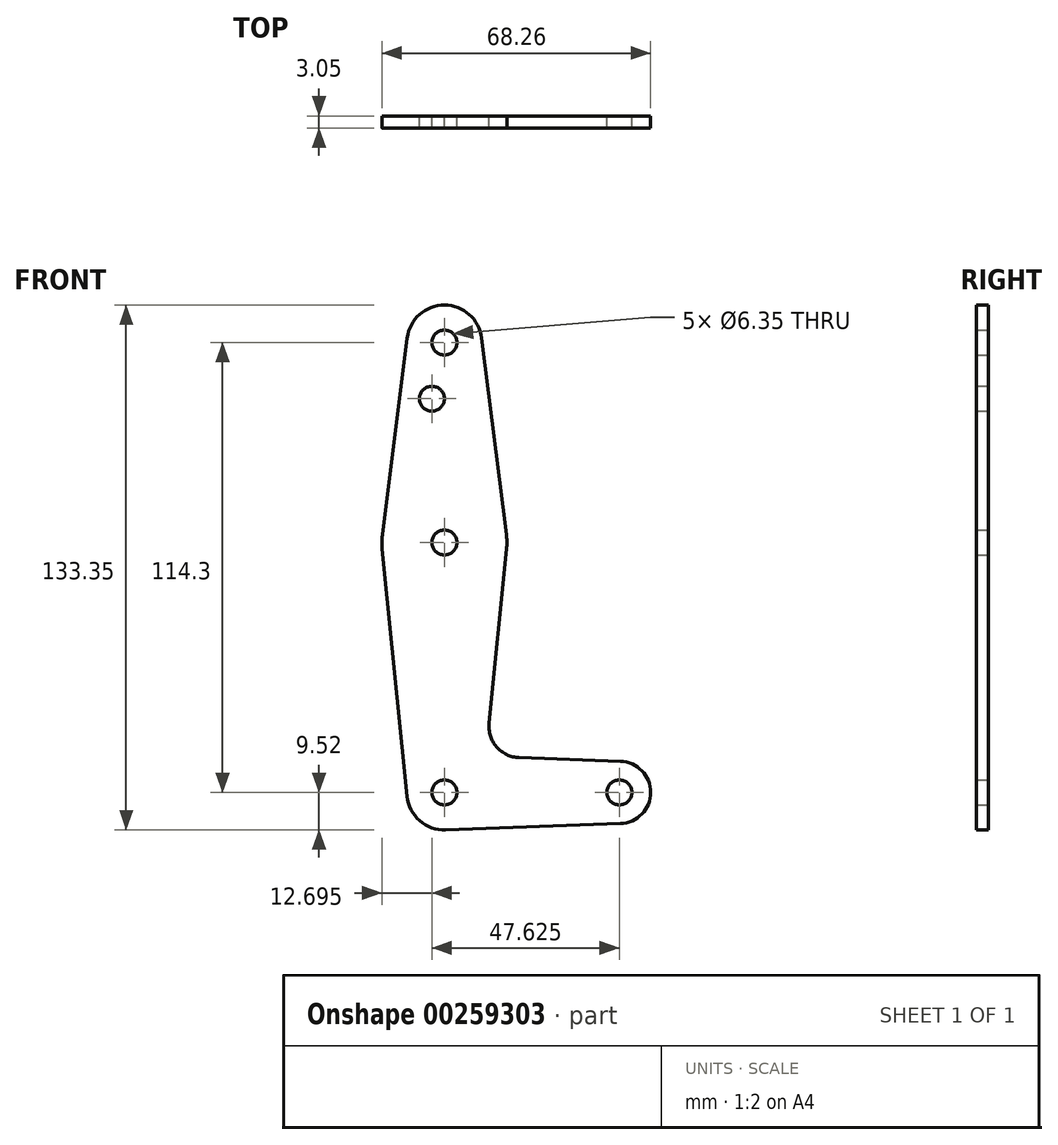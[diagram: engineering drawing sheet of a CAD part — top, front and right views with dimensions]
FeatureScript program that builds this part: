
annotation { "Feature Type Name" : "Feature", "Feature Type Description" : "" }
export const myFeature = defineFeature(function(context is Context, id is Id, definition is map)
    precondition{}
    {
        {
            var Q0;
            Q0=qCreatedBy(makeId("Front.planeOp"),FACE);
            var sketch = newSketch(context, id + "F0", { "sketchPlane" : qUnion([Q0])});
            skLineSegment(sketch, "E0", {"start": v(44.45, 0) * mm, "end": v(0, 0) * mm, "construction": true});
            skLineSegment(sketch, "E1", {"start": v(0, 0) * mm, "end": v(0, 114.3) * mm, "construction": true});
            skCircle(sketch, "E2", {"center": v(44.45, 0) * mm, "radius": 7.94 * mm});
            skCircle(sketch, "E3", {"center": v(0, 0) * mm, "radius": 9.53 * mm});
            skCircle(sketch, "E4", {"center": v(0, 63.5) * mm, "radius": 15.88 * mm});
            skCircle(sketch, "E5", {"center": v(0, 114.3) * mm, "radius": 9.53 * mm});
            skLineSegment(sketch, "E6", {"start": v(-9.45, 115.5) * mm, "end": v(-15.75, 65.48) * mm});
            skLineSegment(sketch, "E7", {"start": v(9.45, 115.5) * mm, "end": v(15.75, 65.48) * mm});
            skLineSegment(sketch, "E8", {"start": v(44.73, 7.93) * mm, "end": v(18.97, 8.85) * mm});
            skLineSegment(sketch, "E9", {"start": v(44.73, -7.93) * mm, "end": v(0, -9.53) * mm});
            skLineSegment(sketch, "E10", {"start": v(-15.8, 61.91) * mm, "end": v(-9.48, -0.95) * mm});
            skLineSegment(sketch, "E11", {"start": v(11.34, 17.6) * mm, "end": v(15.8, 61.91) * mm});
            skCircle(sketch, "E12", {"center": v(44.45, 0) * mm, "radius": 3.18 * mm});
            skCircle(sketch, "E13", {"center": v(0, 0) * mm, "radius": 3.18 * mm});
            skCircle(sketch, "E14", {"center": v(0, 63.5) * mm, "radius": 3.18 * mm});
            skCircle(sketch, "E15", {"center": v(0, 114.3) * mm, "radius": 3.18 * mm});
            skCircle(sketch, "E16", {"center": v(-3.17, 100.03) * mm, "radius": 3.18 * mm});
            skArc(sketch, "E17.filletArc", {"start": v(11.34, 17.6) * mm, "mid": v(13.26, 11.57) * mm, "end": v(18.97, 8.85) * mm});
            skSolve(sketch);
        }
        {
            var Q0;
            Q0=makeQuery(id+"F0.imprint","IMPRINT",FACE,{"disambiguationData":[TD([[makeQuery(id+"F0.imprint","IMPRINT",EDGE,{"derivedFrom":sQuery(id+"F0.wireOp",EDGE,"E15")}),-1.0]])]});
            var Q1;
            {var subQ1=sQuery(id+"F0.wireOp",EDGE,"E6");Q1=makeQuery(id+"F0.imprint","IMPRINT",FACE,{"disambiguationData":[TD([[makeQuery(id+"F0.imprint","IMPRINT",EDGE,{"derivedFrom":subQ1}),1.0]])]});}
            var Q2;
            Q2=makeQuery(id+"F0.imprint","IMPRINT",FACE,{"disambiguationData":[TD([[makeQuery(id+"F0.imprint","IMPRINT",EDGE,{"derivedFrom":sQuery(id+"F0.wireOp",EDGE,"E14")}),-1.0]])]});
            var Q3;
            {var subQ0=sQuery(id+"F0.wireOp",EDGE,"E8");Q3=makeQuery(id+"F0.imprint","IMPRINT",FACE,{"disambiguationData":[TD([[makeQuery(id+"F0.imprint","IMPRINT",EDGE,{"derivedFrom":subQ0}),1.0]])]});}
            var Q4;
            Q4=makeQuery(id+"F0.imprint","IMPRINT",FACE,{"disambiguationData":[TD([[makeQuery(id+"F0.imprint","IMPRINT",EDGE,{"derivedFrom":sQuery(id+"F0.wireOp",EDGE,"E13")}),-1.0]])]});
            var Q5;
            Q5=makeQuery(id+"F0.imprint","IMPRINT",FACE,{"disambiguationData":[TD([[makeQuery(id+"F0.imprint","IMPRINT",EDGE,{"derivedFrom":sQuery(id+"F0.wireOp",EDGE,"E12")}),-1.0]])]});
            extrude(context, id + "F1", {"entities" : qUnion([Q0, Q1, Q2, Q3, Q4, Q5]), "depth" : 3.05 * mm});
        }
    });
